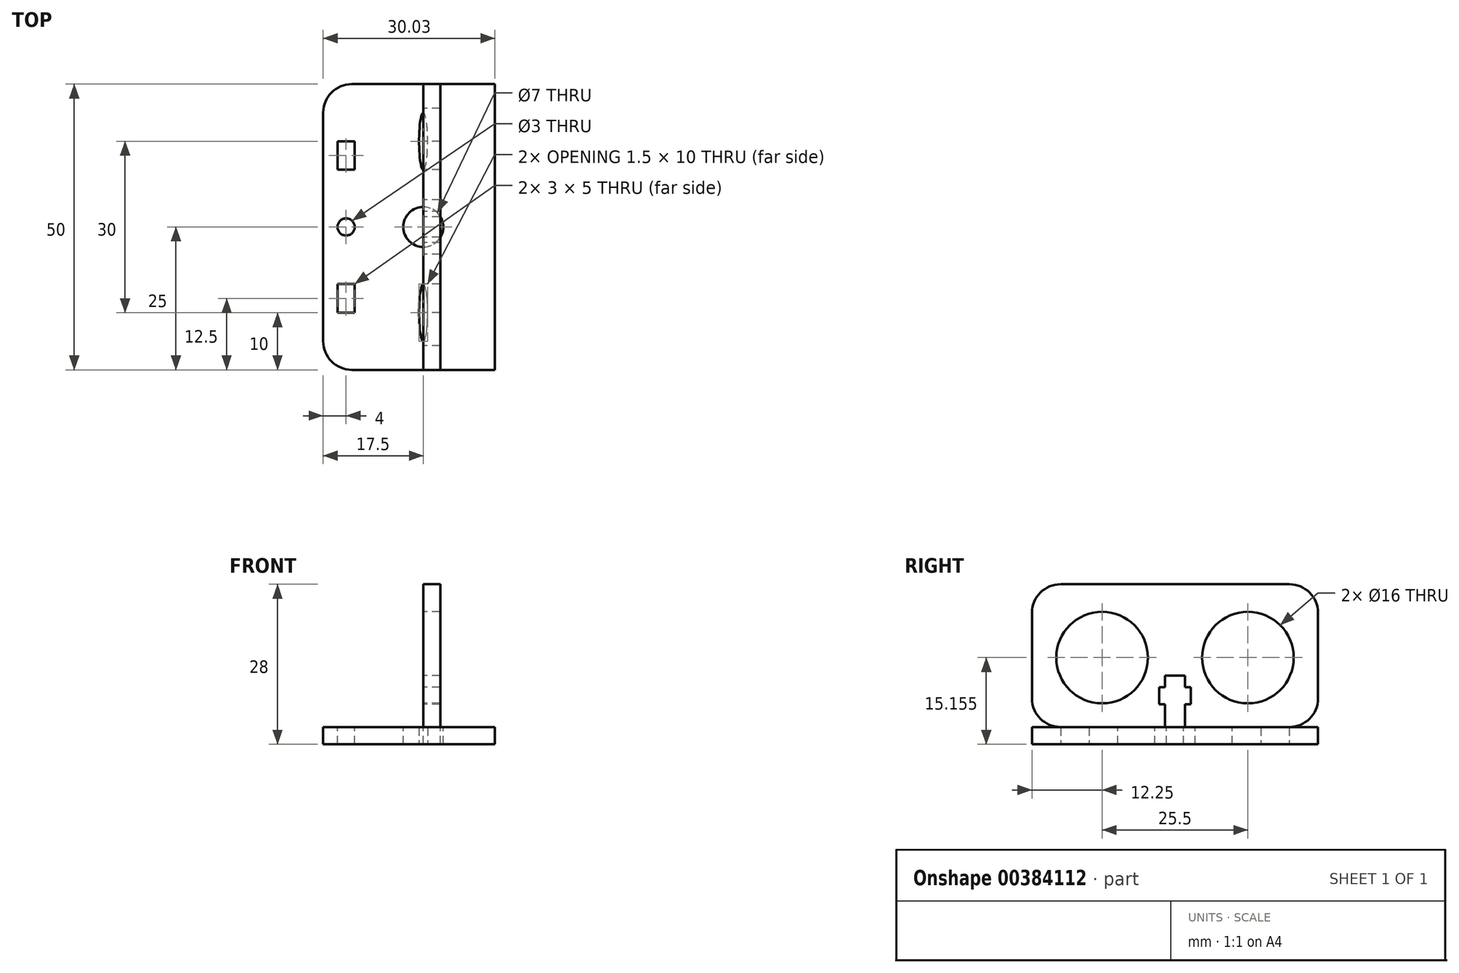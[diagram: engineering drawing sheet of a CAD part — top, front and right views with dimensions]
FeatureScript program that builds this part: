
annotation { "Feature Type Name" : "Feature", "Feature Type Description" : "" }
export const myFeature = defineFeature(function(context is Context, id is Id, definition is map)
    precondition{}
    {
        {
            var Q0;
            Q0=qCreatedBy(makeId("Top.planeOp"),FACE);
            var sketch = newSketch(context, id + "F0", { "sketchPlane" : qUnion([Q0])});
            skLineSegment(sketch, "E0.bottom", {"start": v(-17.5, 25) * mm, "end": v(17.5, 25) * mm});
            skLineSegment(sketch, "E0.top", {"start": v(-17.5, -25) * mm, "end": v(17.5, -25) * mm});
            skLineSegment(sketch, "E0.left", {"start": v(-17.5, 25) * mm, "end": v(-17.5, -25) * mm});
            skLineSegment(sketch, "E0.right", {"start": v(17.5, 25) * mm, "end": v(17.5, -25) * mm});
            skPoint(sketch, "E0.middle", {"position": v(0, 0) * mm});
            skSolve(sketch);
        }
        {
            var Q0;
            Q0=makeQuery(id+"F0.imprint","IMPRINT",FACE,{"disambiguationData":[TD([[makeQuery(id+"F0.imprint","IMPRINT",EDGE,{"derivedFrom":sQuery(id+"F0.wireOp",EDGE,"E0.bottom")}),-1.0]])]});
            extrude(context, id + "F1", {"entities" : qUnion([Q0]), "depth" : 3 * mm});
        }
        {
            var Q0;
            Q0=makeQuery(id+"F1.opExtrude","CAP_FACE",FACE,{"disambiguationData":[OSD([sQuery(id+"F0.wireOp",EDGE,"E0.bottom"),sQuery(id+"F0.wireOp",EDGE,"E0.top"),sQuery(id+"F0.wireOp",EDGE,"E0.left"),sQuery(id+"F0.wireOp",EDGE,"E0.right")])],"isStart":false});
            var sketch = newSketch(context, id + "F2", { "sketchPlane" : qUnion([Q0])});
            skLineSegment(sketch, "E1.bottom", {"start": v(-12, -15) * mm, "end": v(-15, -15) * mm});
            skLineSegment(sketch, "E1.top", {"start": v(-12, -10) * mm, "end": v(-15, -10) * mm});
            skLineSegment(sketch, "E1.left", {"start": v(-12, -15) * mm, "end": v(-12, -10) * mm});
            skLineSegment(sketch, "E1.right", {"start": v(-15, -15) * mm, "end": v(-15, -10) * mm});
            skPoint(sketch, "E1.middle", {"position": v(-13.5, -12.5) * mm});
            skLineSegment(sketch, "E2.MirrorCS", {"start": v(-12, 15) * mm, "end": v(-15, 15) * mm});
            skPoint(sketch, "E3.MirrorP", {"position": v(-13.5, 12.5) * mm});
            skLineSegment(sketch, "E4.MirrorCS", {"start": v(-12, 10) * mm, "end": v(-15, 10) * mm});
            skLineSegment(sketch, "E5.MirrorCS", {"start": v(-15, 15) * mm, "end": v(-15, 10) * mm});
            skLineSegment(sketch, "E6.MirrorCS", {"start": v(-12, 15) * mm, "end": v(-12, 10) * mm});
            skCircle(sketch, "E7", {"center": v(-13.5, 0) * mm, "radius": 1.5 * mm});
            skCircle(sketch, "E8", {"center": v(0, 0) * mm, "radius": 3.5 * mm});
            skLineSegment(sketch, "E9", {"start": v(-13.5, -12.5) * mm, "end": v(-13.5, 12.5) * mm, "construction": true});
            skEllipse(sketch, "E10", {"center": v(0, -15) * mm, "majorRadius": 5 * mm, "minorRadius": 0.75 * mm, "majorAxis": v(0, 1)});
            skEllipse(sketch, "E11.MirrorC", {"center": v(0, 15) * mm, "majorRadius": 5 * mm, "minorRadius": 0.75 * mm, "majorAxis": v(0, -1)});
            skLineSegment(sketch, "E12.bottom", {"start": v(17.5, 25) * mm, "end": v(12.53, 25) * mm});
            skLineSegment(sketch, "E12.top", {"start": v(17.5, -25) * mm, "end": v(12.53, -25) * mm});
            skLineSegment(sketch, "E12.left", {"start": v(17.5, 25) * mm, "end": v(17.5, -25) * mm});
            skLineSegment(sketch, "E12.right", {"start": v(12.53, 25) * mm, "end": v(12.53, -25) * mm});
            skSolve(sketch);
        }
        {
            var Q0;
            Q0=qSketchRegion(id+"F2",true);
            extrude(context, id + "F3", {"entities" : qUnion([Q0]), "operationType" : NewBodyOperationType.REMOVE, "oppositeDirection" : true, "depth" : 25 * mm});
        }
        {
            var Q0;
            Q0=qCreatedBy(makeId("Right.planeOp"),FACE);
            var sketch = newSketch(context, id + "F4", { "sketchPlane" : qUnion([Q0])});
            skLineSegment(sketch, "E13.bottom", {"start": v(-25, 3) * mm, "end": v(-15, 3) * mm});
            skLineSegment(sketch, "E13.top", {"start": v(-25, 28) * mm, "end": v(25, 28) * mm});
            skLineSegment(sketch, "E13.left", {"start": v(-25, 3) * mm, "end": v(-25, 28) * mm});
            skLineSegment(sketch, "E13.right", {"start": v(25, 3) * mm, "end": v(25, 28) * mm});
            skCircle(sketch, "E14", {"center": v(-12.75, 15.16) * mm, "radius": 8 * mm});
            skCircle(sketch, "E15.MirrorC", {"center": v(12.75, 15.16) * mm, "radius": 8 * mm});
            skLineSegment(sketch, "E16", {"start": v(-15, 3) * mm, "end": v(-15, 0) * mm});
            skLineSegment(sketch, "E17", {"start": v(-15, 0) * mm, "end": v(-10, 0) * mm});
            skLineSegment(sketch, "E18", {"start": v(-10, 0) * mm, "end": v(-10, 3) * mm});
            skLineSegment(sketch, "E19.trimOffspring", {"start": v(-10, 3) * mm, "end": v(10, 3) * mm});
            skLineSegment(sketch, "E20.MirrorCS", {"start": v(10, 0) * mm, "end": v(10, 3) * mm});
            skLineSegment(sketch, "E21.MirrorCS", {"start": v(15, 0) * mm, "end": v(10, 0) * mm});
            skLineSegment(sketch, "E22.MirrorCS", {"start": v(15, 3) * mm, "end": v(15, 0) * mm});
            skLineSegment(sketch, "E23.trimOffspring", {"start": v(15, 3) * mm, "end": v(25, 3) * mm});
            skLineSegment(sketch, "E24.bottom", {"start": v(-1.75, 3) * mm, "end": v(1.75, 3) * mm});
            skLineSegment(sketch, "E24.top", {"start": v(-1.75, 12) * mm, "end": v(1.75, 12) * mm});
            skLineSegment(sketch, "E24.left", {"start": v(-1.75, 3) * mm, "end": v(-1.75, 7) * mm});
            skLineSegment(sketch, "E24.right", {"start": v(1.75, 3) * mm, "end": v(1.75, 7) * mm});
            skLineSegment(sketch, "E25.bottom", {"start": v(-2.75, 7) * mm, "end": v(-1.75, 7) * mm});
            skLineSegment(sketch, "E25.top", {"start": v(-2.75, 10) * mm, "end": v(-1.75, 10) * mm});
            skLineSegment(sketch, "E25.left", {"start": v(-2.75, 7) * mm, "end": v(-2.75, 10) * mm});
            skLineSegment(sketch, "E25.right", {"start": v(2.75, 7) * mm, "end": v(2.75, 10) * mm});
            skLineSegment(sketch, "E26.trimOffspring", {"start": v(1.75, 10) * mm, "end": v(2.75, 10) * mm});
            skLineSegment(sketch, "E27.trimOffspring", {"start": v(-1.75, 10) * mm, "end": v(-1.75, 12) * mm});
            skLineSegment(sketch, "E28.trimOffspring", {"start": v(1.75, 10) * mm, "end": v(1.75, 12) * mm});
            skLineSegment(sketch, "E29.trimOffspring", {"start": v(1.75, 7) * mm, "end": v(2.75, 7) * mm});
            skSolve(sketch);
        }
        {
            var Q0;
            Q0=makeQuery(id+"F4.imprint","IMPRINT",FACE,{"disambiguationData":[TD([[makeQuery(id+"F4.imprint","IMPRINT",EDGE,{"derivedFrom":sQuery(id+"F4.wireOp",EDGE,"E13.bottom")}),1.0]])]});
            extrude(context, id + "F5", {"entities" : qUnion([Q0]), "depth" : 3 * mm});
        }
        {
            var Q0;
            Q0=makeQuery(id+"F3.boolean.opBoolean","COPY",EDGE,{"derivedFrom":makeQuery(id+"F3.opExtrude","SWEPT_EDGE",EDGE,{"disambiguationData":[OSD([sQuery(id+"F0.wireOp",EDGE,"E0.bottom"),sQuery(id+"F2.wireOp",EDGE,"E12.bottom"),sQuery(id+"F2.wireOp",EDGE,"E12.right")])]})});
            var Q1;
            Q1=makeQuery(id+"F3.boolean.opBoolean","COPY",EDGE,{"derivedFrom":makeQuery(id+"F3.opExtrude","SWEPT_EDGE",EDGE,{"disambiguationData":[OSD([sQuery(id+"F0.wireOp",EDGE,"E0.top"),sQuery(id+"F2.wireOp",EDGE,"E12.top"),sQuery(id+"F2.wireOp",EDGE,"E12.right")])]})});
            var Q2;
            Q2=makeQuery(id+"F1.opExtrude","SWEPT_EDGE",EDGE,{"disambiguationData":[OSD([sQuery(id+"F0.wireOp",EDGE,"E0.top"),sQuery(id+"F0.wireOp",EDGE,"E0.left")])]});
            var Q3;
            Q3=makeQuery(id+"F1.opExtrude","SWEPT_EDGE",EDGE,{"disambiguationData":[OSD([sQuery(id+"F0.wireOp",EDGE,"E0.bottom"),sQuery(id+"F0.wireOp",EDGE,"E0.left")])]});
            fillet(context, id + "F6", {"entities" : qUnion([Q0, Q1, Q2, Q3]), "radius" : 5 * mm, "tangentPropagation" : true, "allowEdgeOverflow" : false});
        }
        {
            var Q0;
            Q0=makeQuery(id+"F5.opExtrude","SWEPT_EDGE",EDGE,{"disambiguationData":[OSD([sQuery(id+"F4.wireOp",EDGE,"E13.bottom"),sQuery(id+"F4.wireOp",EDGE,"E13.left")])]});
            var Q1;
            Q1=makeQuery(id+"F5.opExtrude","SWEPT_EDGE",EDGE,{"disambiguationData":[OSD([sQuery(id+"F4.wireOp",EDGE,"E13.top"),sQuery(id+"F4.wireOp",EDGE,"E13.left")])]});
            var Q2;
            Q2=makeQuery(id+"F5.opExtrude","SWEPT_EDGE",EDGE,{"disambiguationData":[OSD([sQuery(id+"F4.wireOp",EDGE,"E13.top"),sQuery(id+"F4.wireOp",EDGE,"E13.right")])]});
            var Q3;
            Q3=makeQuery(id+"F5.opExtrude","SWEPT_EDGE",EDGE,{"disambiguationData":[OSD([sQuery(id+"F4.wireOp",EDGE,"E13.right"),sQuery(id+"F4.wireOp",EDGE,"E23.trimOffspring")])]});
            fillet(context, id + "F7", {"entities" : qUnion([Q0, Q1, Q2, Q3]), "radius" : 5 * mm, "tangentPropagation" : true, "allowEdgeOverflow" : false});
        }
    });
